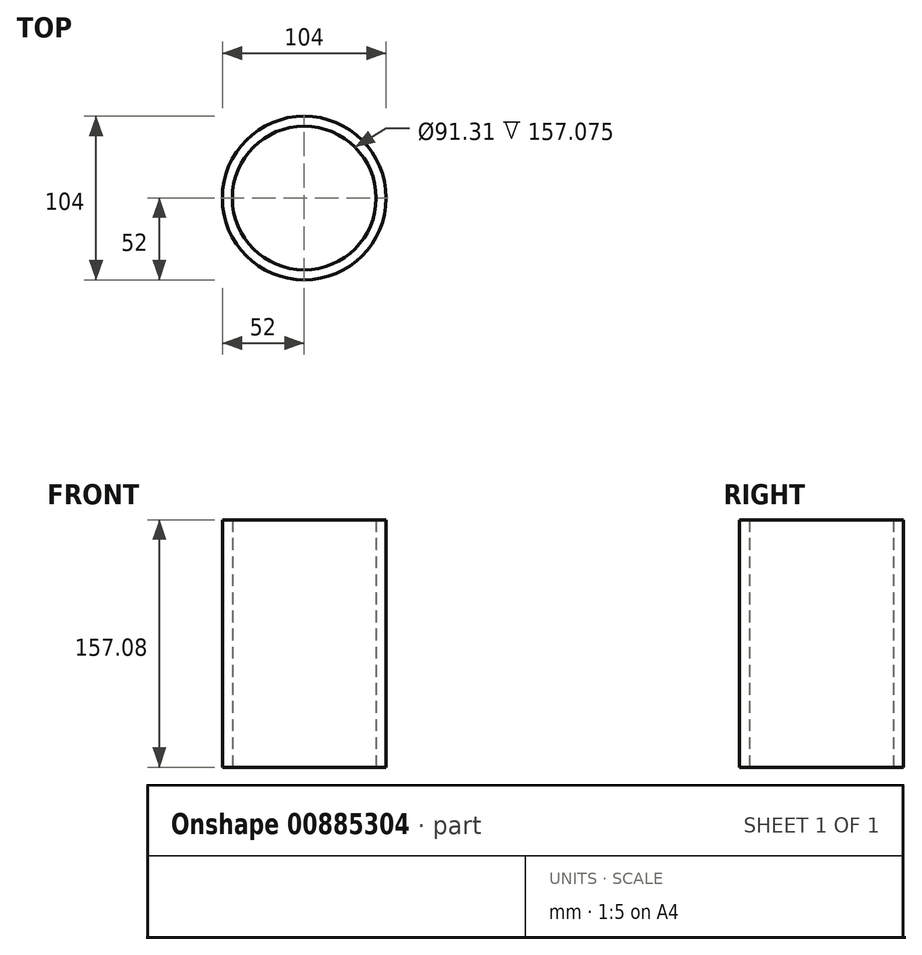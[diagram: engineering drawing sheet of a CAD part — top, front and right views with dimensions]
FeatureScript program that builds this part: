
annotation { "Feature Type Name" : "Feature", "Feature Type Description" : "" }
export const myFeature = defineFeature(function(context is Context, id is Id, definition is map)
    precondition{}
    {
        {
            var Q0;
            Q0=qCreatedBy(makeId("Top.planeOp"),FACE);
            var sketch = newSketch(context, id + "F0", { "sketchPlane" : qUnion([Q0])});
            skCircle(sketch, "E0", {"center": v(0, 0) * mm, "radius": 45.65 * mm});
            skCircle(sketch, "E1.0", {"center": v(0, 0) * mm, "radius": 52 * mm});
            skSolve(sketch);
        }
        {
            var Q0;
            Q0=makeQuery(id+"F0.imprint","IMPRINT",FACE,{"disambiguationData":[TD([[makeQuery(id+"F0.imprint","IMPRINT",EDGE,{"derivedFrom":sQuery(id+"F0.wireOp",EDGE,"E0")}),-1.0]])]});
            extrude(context, id + "F1", {"entities" : qUnion([Q0]), "depth" : 157.08 * mm, "offsetDistance" : 25.4 * mm});
        }
    });
